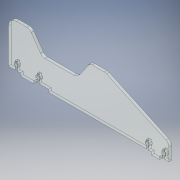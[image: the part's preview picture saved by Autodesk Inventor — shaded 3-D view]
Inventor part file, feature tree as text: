
AUTODESK INVENTOR PART (.ipt)
format: ipt  version: 2019 (Build 230136000, 136)  size: 240,128 bytes
history: native  units: mm
features: fillet x3, extrude x1, sketch x1
ambient origin geometry x8: Origin, YZ Plane, XZ Plane, XY Plane, X Axis, Y Axis, Z Axis, Center Point
bodies: Solid1 (feature_tree)
feature tree (5):
  extrude  "Extrusion1"  Depth=110.5mm
  fillet  "Fillet1"  Radius=80.0mm
  fillet  "Fillet2"  Radius=75.0mm
  fillet  "Fillet3"  Radius=189.5mm
  sketch  "Sketch1"  dims[d0=127.0mm d1=110.5mm d2=80.0mm d3=75.0mm d4=189.5mm d5=85.0mm d6=55.0mm d7=25.0mm d8=5.0mm d9=27.5mm d10=15.0mm d11=5.0mm d13=67.0mm d14=5.0mm d15=5.0mm d16=0.0mm d17=10.0mm d18=15.0mm d19=30.0mm d20=30.0mm d21=17.5mm d23=6.0mm d24=4.0mm d25=15.0mm d26=8.0mm d27=4.0mm d28=7.0mm d29=4.0mm d30=8.0mm d31=7.0mm d32=6.0mm d33=4.0mm d34=15.0mm d35=6.0mm d36=4.0mm d37=15.0mm d38=6.0mm d39=8.0mm d40=4.0mm d41=8.0mm d42=7.0mm d43=7.0mm d44=7.0mm d45=7.0mm d46=12.5mm d47=30.0mm d48=10.0mm]
